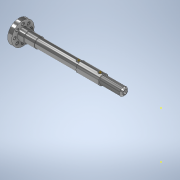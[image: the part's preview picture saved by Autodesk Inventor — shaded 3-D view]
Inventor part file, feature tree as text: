
AUTODESK INVENTOR PART (.ipt)
format: ipt  version: 2022 (Build 260153000, 153)  size: 272,384 bytes
history: native  units: in
note: dims shown in document units (in); Inventor stores cm internally (conversion verified against a paired STEP export)
features: sketch x10, plane x5, extrude x4, other x4, revolve x3, chamfer x3, thread x2
ambient origin geometry x8: Origin, YZ Plane, XZ Plane, XY Plane, X Axis, Y Axis, Z Axis, Center Point
bodies: Solid1 (feature_tree)
feature tree (31):
  revolve  "Revolution1"  [1 undecoded]
  plane  "Work Plane2"
  extrude  "Extrusion1"  Depth=0.8465in
  sketch  "Sketch4"  dims[d12=0.4331in d13=0.3465in]
  extrude  "Extrusion2"  Depth=0.3465in
  sketch  "Sketch6"  dims[d16=0.3819in d17=0.3819in]
  plane  "Work Plane3"
  revolve  "Revolution2"  [1 undecoded]
  revolve  "Revolution3"  [1 undecoded]
  extrude  "Extrusion8"  TaperAngle=90.0deg  [1 undecoded]
  chamfer  "Chamfer1"  Distance=0.1732in
  chamfer  "Chamfer2"  Distance=1.7913in
  plane  "Work Plane5"
  extrude  "Extrusion9"  TaperAngle=90.0deg  [1 undecoded]
  chamfer  "Chamfer3"  Distance=0.8661in
  sketch  "Sketch18"  dims[d39=0.6299in d40=0.8661in d41=120.0deg d42=0.2874in d43=0.315in d44=0.1063in d45=3.1496in d47=360.0deg d49=0.3937in d50=0.0in d51=0.0079in d52=0.0787in d53=45.0deg d54=0.063in d55=0.0787in d56=45.0deg d57=-0.9646in d58=0.0984in d59=0.3937in d60=0.0in d61=0.0197in d62=0.0787in d63=45.0deg d66=0.7835in d67=0.0in d68=0.1098in d69=0.0in]
  thread  "Thread1"  [1 undecoded]
  thread  "Thread2"  [1 undecoded]
  sketch  "Sketch2"  dims[d8=4.1142in d9=3.9567in]
  plane  "Work Plane1"
  other  "Work Axis1"
  other  "Work Point1"
  sketch  "Sketch3"  dims[d10=3.7205in d11=0.8465in]
  sketch  "Sketch5"  dims[d14=3.3268in d15=1.7126in]
  sketch  "Sketch10"  dims[d18=0.315in d19=90.0deg]
  sketch  "Sketch14"  dims[d20=-1.7913in d21=0.1732in d22=0.0in d23=1.7913in d24=0.0in]
  sketch  "Sketch15"  dims[d26=90.0deg d37=90.0deg]
  plane  "Work Plane4"
  other  "Work Axis2"
  other  "Work Point2"
  sketch  "Sketch16"  dims[d38=90.0deg]
note: 7 required parameter values undecoded (feature->parameter linkage not recoverable at this tier; creation-order binding heuristic only, values carry confidence <= 0.55)